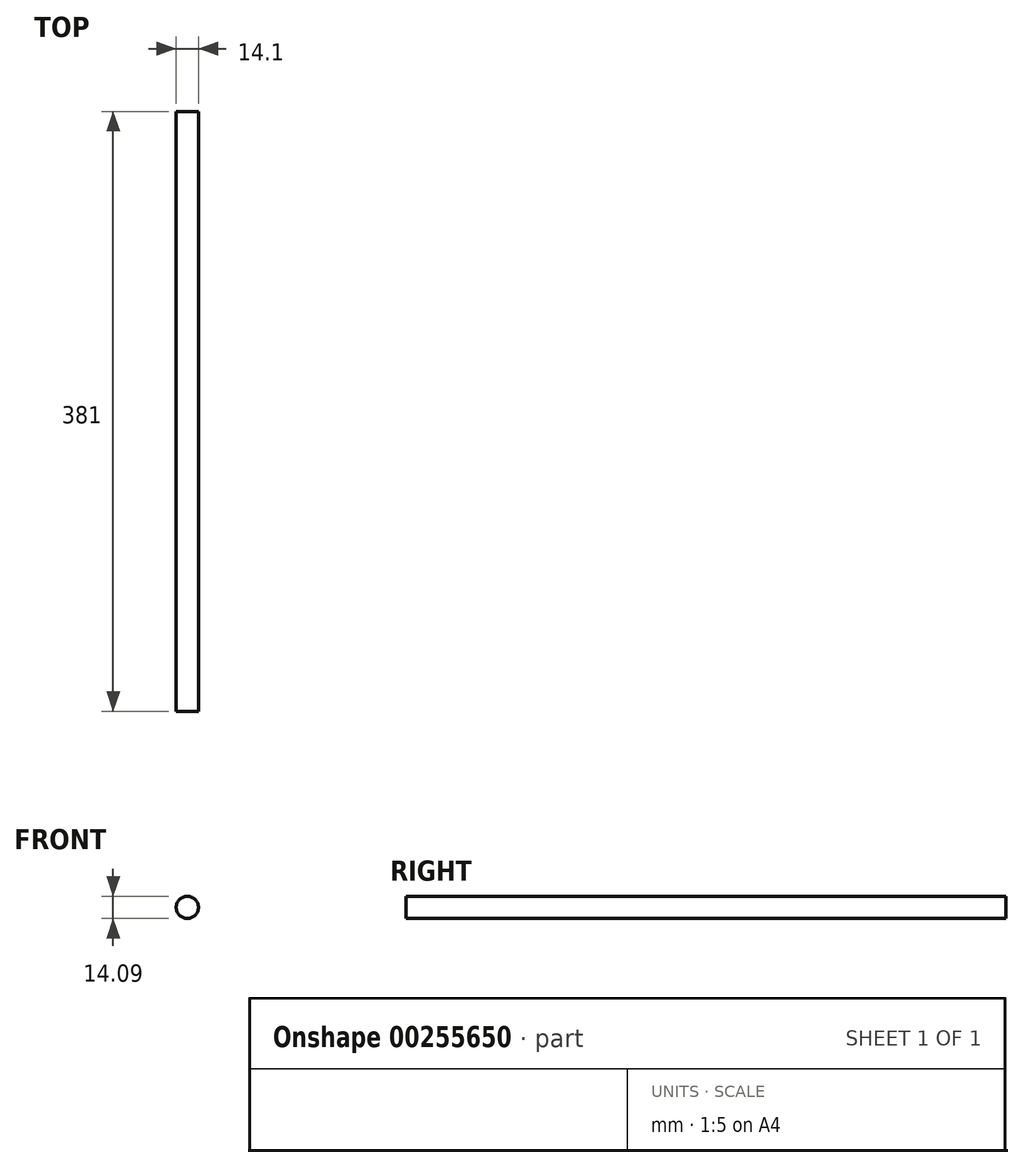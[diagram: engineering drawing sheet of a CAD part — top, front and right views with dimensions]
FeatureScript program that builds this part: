
annotation { "Feature Type Name" : "Feature", "Feature Type Description" : "" }
export const myFeature = defineFeature(function(context is Context, id is Id, definition is map)
    precondition{}
    {
        {
            var Q0;
            Q0=qCreatedBy(makeId("Front.planeOp"),FACE);
            var sketch = newSketch(context, id + "F0", { "sketchPlane" : qUnion([Q0])});
            skCircle(sketch, "E0", {"center": v(0, 38.59) * mm, "radius": 7.05 * mm});
            skSolve(sketch);
        }
        {
            var Q0;
            Q0=sQuery(id+"F0.wireOp",EDGE,"E0");
            extrude(context, id + "F1", {"bodyType" : ToolBodyType.SURFACE, "surfaceEntities" : qUnion([Q0]), "depth" : 381 * mm});
        }
        {
            var Q0;
            Q0=qCreatedBy(makeId("Right.planeOp"),FACE);
            var sketch = newSketch(context, id + "F2", { "sketchPlane" : qUnion([Q0])});
            skLineSegment(sketch, "E1", {"start": v(0, 36.55) * mm, "end": v(0, -79.45) * mm});
            skLineSegment(sketch, "E2", {"start": v(0, -79.45) * mm, "end": v(-376.05, 30.59) * mm});
            skSolve(sketch);
        }
    });
